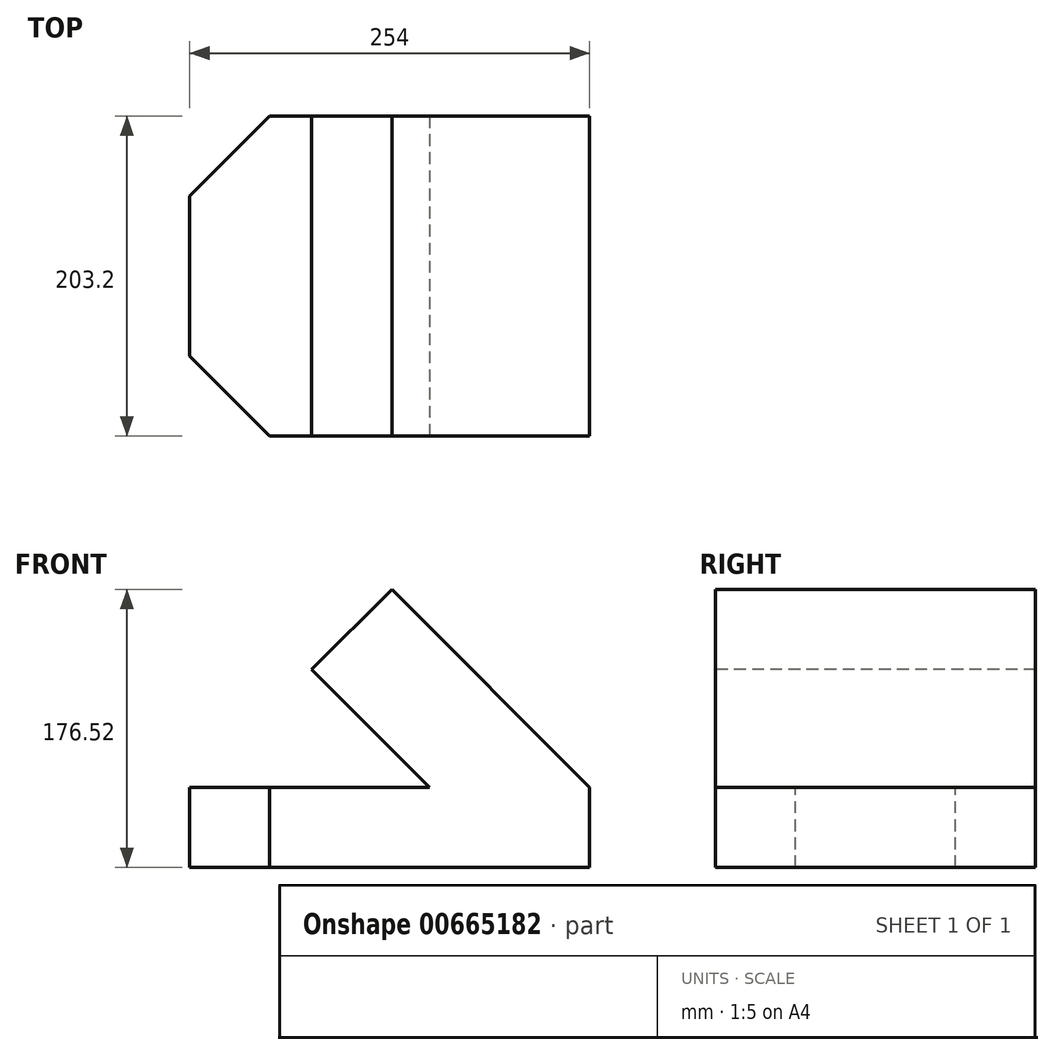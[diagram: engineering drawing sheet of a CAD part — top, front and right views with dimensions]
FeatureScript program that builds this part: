
annotation { "Feature Type Name" : "Feature", "Feature Type Description" : "" }
export const myFeature = defineFeature(function(context is Context, id is Id, definition is map)
    precondition{}
    {
        {
            var Q0;
            Q0=qCreatedBy(makeId("Front.planeOp"),FACE);
            var sketch = newSketch(context, id + "F0", { "sketchPlane" : qUnion([Q0])});
            skLineSegment(sketch, "E0", {"start": v(0, 0) * mm, "end": v(-254, 0) * mm});
            skLineSegment(sketch, "E1", {"start": v(-254, 0) * mm, "end": v(-254, 50.8) * mm});
            skLineSegment(sketch, "E2", {"start": v(-254, 50.8) * mm, "end": v(-101.6, 50.8) * mm});
            skLineSegment(sketch, "E3", {"start": v(-101.6, 50.8) * mm, "end": v(-176.52, 125.72) * mm});
            skLineSegment(sketch, "E4", {"start": v(-176.52, 125.72) * mm, "end": v(-125.72, 176.52) * mm});
            skLineSegment(sketch, "E5", {"start": v(-125.72, 176.52) * mm, "end": v(0, 50.8) * mm});
            skLineSegment(sketch, "E6", {"start": v(0, 50.8) * mm, "end": v(0, 0) * mm});
            skSolve(sketch);
        }
        {
            var Q0;
            Q0=makeQuery(id+"F0.imprint","IMPRINT",FACE,{"disambiguationData":[TD([[makeQuery(id+"F0.imprint","IMPRINT",EDGE,{"derivedFrom":sQuery(id+"F0.wireOp",EDGE,"E0")}),-1.0]])]});
            extrude(context, id + "F1", {"entities" : qUnion([Q0]), "oppositeDirection" : true, "depth" : 203.2 * mm, "offsetDistance" : 25.4 * mm});
        }
        {
            var Q0;
            Q0=makeQuery(id+"F1.opExtrude","SWEPT_FACE",FACE,{"disambiguationData":[OSD([sQuery(id+"F0.wireOp",EDGE,"E5")])]});
            var sketch = newSketch(context, id + "F2", { "sketchPlane" : qUnion([Q0])});
            skCircle(sketch, "E7", {"center": v(-162.92, 101.6) * mm, "radius": 38.1 * mm});
            skSolve(sketch);
        }
        {
            var Q0;
            Q0=makeQuery(id+"F2.imprint","IMPRINT",FACE,{"disambiguationData":[TD([[makeQuery(id+"F2.imprint","IMPRINT",EDGE,{"derivedFrom":sQuery(id+"F2.wireOp",EDGE,"E7")}),1.0]])]});
            extrude(context, id + "F3", {"entities" : qUnion([Q0]), "operationType" : NewBodyOperationType.REMOVE, "oppositeDirection" : true, "depth" : 76.2 * mm, "offsetDistance" : 25.4 * mm});
        }
        {
            var Q0;
            Q0=makeQuery(id+"F1.opExtrude","SWEPT_FACE",FACE,{"disambiguationData":[OSD([sQuery(id+"F0.wireOp",EDGE,"E2")])]});
            var sketch = newSketch(context, id + "F4", { "sketchPlane" : qUnion([Q0])});
            skLineSegment(sketch, "E8", {"start": v(-254, 0) * mm, "end": v(-203.2, 0) * mm});
            skLineSegment(sketch, "E9", {"start": v(-203.2, 0) * mm, "end": v(-254, 50.8) * mm});
            skLineSegment(sketch, "E10", {"start": v(-254, 50.8) * mm, "end": v(-254, 0) * mm});
            skLineSegment(sketch, "E11", {"start": v(-254, 203.2) * mm, "end": v(-203.2, 203.2) * mm});
            skLineSegment(sketch, "E12", {"start": v(-203.2, 203.2) * mm, "end": v(-254, 152.4) * mm});
            skLineSegment(sketch, "E13", {"start": v(-254, 152.4) * mm, "end": v(-254, 203.2) * mm});
            skSolve(sketch);
        }
        {
            var Q0;
            Q0=makeQuery(id+"F4.imprint","IMPRINT",FACE,{"disambiguationData":[TD([[makeQuery(id+"F4.imprint","IMPRINT",EDGE,{"derivedFrom":sQuery(id+"F4.wireOp",EDGE,"E11")}),-1.0]])]});
            var Q1;
            Q1=makeQuery(id+"F4.imprint","IMPRINT",FACE,{"disambiguationData":[TD([[makeQuery(id+"F4.imprint","IMPRINT",EDGE,{"derivedFrom":sQuery(id+"F4.wireOp",EDGE,"E8")}),1.0]])]});
            extrude(context, id + "F5", {"entities" : qUnion([Q0, Q1]), "operationType" : NewBodyOperationType.REMOVE, "oppositeDirection" : true, "depth" : 50.8 * mm, "offsetDistance" : 25.4 * mm});
        }
    });
